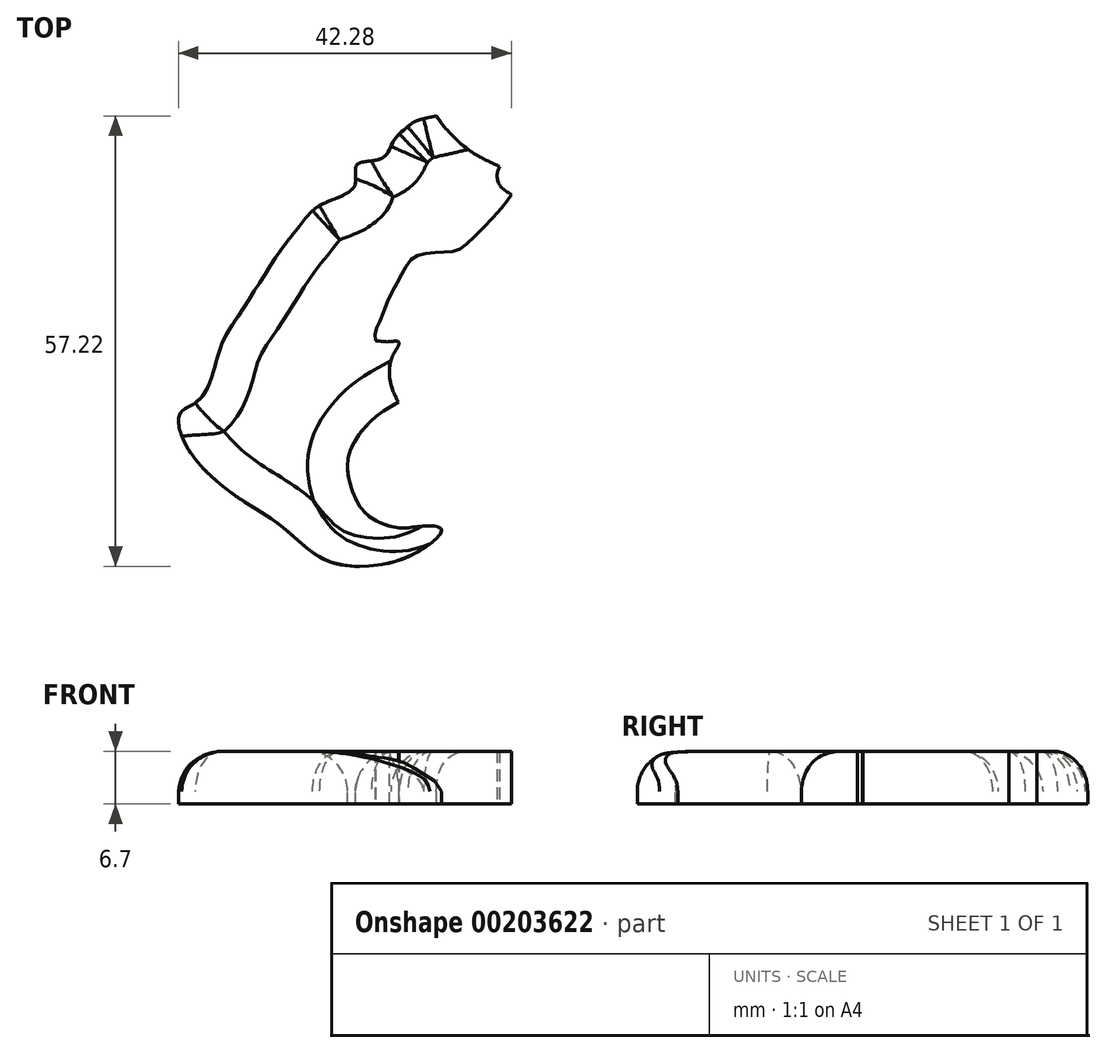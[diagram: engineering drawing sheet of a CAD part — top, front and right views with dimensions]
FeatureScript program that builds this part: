
annotation { "Feature Type Name" : "Feature", "Feature Type Description" : "" }
export const myFeature = defineFeature(function(context is Context, id is Id, definition is map)
    precondition{}
    {
        {
            var Q0;
            Q0=qCreatedBy(makeId("Top.planeOp"),FACE);
            var sketch = newSketch(context, id + "F0", { "sketchPlane" : qUnion([Q0])});
            skFitSpline(sketch, "E0", {"points": [v(-21.97, 13.11) * mm, v(-23.26, 12.82) * mm, v(-24.61, 12.4) * mm, v(-25.84, 11.53) * mm, v(-27.37, 9.94) * mm, v(-28.3, 8.19) * mm, v(-29.95, 7.42) * mm, v(-31.94, 7.01) * mm, v(-32.23, 5.9) * mm, v(-32.23, 4.55) * mm, v(-32.59, 3.85) * mm, v(-33.88, 2.97) * mm, v(-35.64, 2.26) * mm, v(-37.51, 1.2) * mm, v(-39.62, -1.26) * mm, v(-41.68, -3.9) * mm, v(-43.55, -6.77) * mm, v(-45.31, -9.52) * mm, v(-47.01, -12.16) * mm, v(-48.83, -15.06) * mm, v(-49.88, -18) * mm, v(-50.72, -20.73) * mm, v(-52.4, -23.25) * mm, v(-54.5, -24.72) * mm, v(-54.08, -28.09) * mm, v(-51.77, -31.45) * mm, v(-47.36, -35.23) * mm, v(-41.9, -38.8) * mm, v(-36.23, -43.21) * mm, v(-30.35, -44.05) * mm, v(-24.46, -42.37) * mm, v(-21.31, -39.43) * mm, v(-23.83, -39.01) * mm, v(-26.77, -39.22) * mm, v(-30.77, -37.54) * mm, v(-32.66, -34.39) * mm, v(-33.08, -29.98) * mm, v(-29.93, -25.35) * mm, v(-26.77, -23.25) * mm], "startDerivative": vector(-73.41, -16.73) * mm, "endDerivative": vector(105.77, 58.5) * mm});
            skFitSpline(sketch, "E1", {"points": [v(-26.77, -23.25) * mm, v(-27.78, -20.74) * mm, v(-27.7, -17.9) * mm, v(-26.77, -16.14) * mm], "startDerivative": vector(-3.53, 6.9) * mm, "endDerivative": vector(3.63, 5.35) * mm});
            skFitSpline(sketch, "E2", {"points": [v(-26.77, -16.14) * mm, v(-26.77, -15.58) * mm, v(-27.86, -15.58) * mm, v(-29.67, -15.44) * mm], "startDerivative": vector(0.69, 2.9) * mm, "endDerivative": vector(-4.22, 0.63) * mm});
            skFitSpline(sketch, "E3", {"points": [v(-29.67, -15.44) * mm, v(-29.67, -14.32) * mm, v(-29.02, -12.8) * mm, v(-27.81, -9.68) * mm, v(-26.37, -7.12) * mm, v(-25.16, -5.13) * mm, v(-23.54, -4.43) * mm, v(-20.98, -4.2) * mm, v(-19.12, -3.87) * mm, v(-17.13, -2.25) * mm, v(-13.67, 1.4) * mm, v(-12.43, 3.13) * mm], "startDerivative": vector(-1.97, 17.96) * mm, "endDerivative": vector(11.49, 18.08) * mm});
            skFitSpline(sketch, "E4", {"points": [v(-12.43, 3.13) * mm, v(-13.75, 4.12) * mm, v(-14.24, 5.51) * mm, v(-13.91, 6.66) * mm], "startDerivative": vector(-4.11, 2.37) * mm, "endDerivative": vector(1.58, 3.6) * mm});
            skFitSpline(sketch, "E5", {"points": [v(-21.97, 13.11) * mm, v(-20.57, 11.29) * mm, v(-17.72, 8.7) * mm, v(-13.91, 6.66) * mm], "startDerivative": vector(4.57, -6.43) * mm, "endDerivative": vector(10.53, -4.9) * mm});
            skSolve(sketch);
        }
        {
            var Q0;
            Q0=makeQuery(id+"F0.imprint","IMPRINT",FACE,{"disambiguationData":[TD([[makeQuery(id+"F0.imprint","IMPRINT",EDGE,{"derivedFrom":sQuery(id+"F0.wireOp",EDGE,"E0")}),1.0]])]});
            extrude(context, id + "F1", {"entities" : qUnion([Q0]), "endBound" : BoundingType.SYMMETRIC, "depth" : 6.7 * mm});
        }
        {
            var Q0;
            Q0=makeQuery(id+"F1.opExtrude","CAP_EDGE",EDGE,{"disambiguationData":[OSD([sQuery(id+"F0.wireOp",EDGE,"E0")])],"isStart":false});
            fillet(context, id + "F2", {"entities" : qUnion([Q0]), "radius" : 5.08 * mm, "tangentPropagation" : true, "allowEdgeOverflow" : false});
        }
    });
